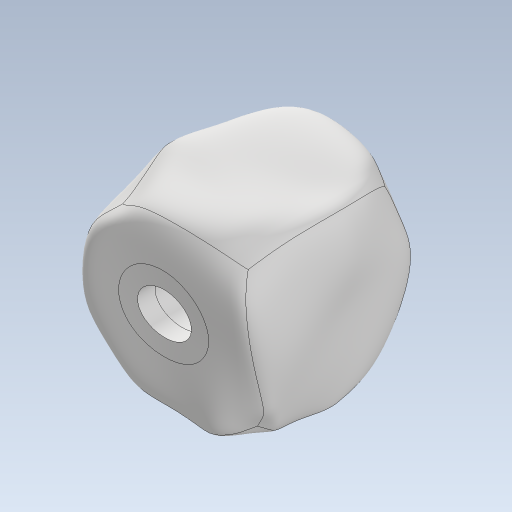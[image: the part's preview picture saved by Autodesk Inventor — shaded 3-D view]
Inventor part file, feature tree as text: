
AUTODESK INVENTOR PART (.ipt)
format: ipt  version: 2023 (Build 270158030, 158C)  size: 744,960 bytes
history: native  units: mm
features: other x4, plane x2, revolve x1, surface_op x1, extrude x1, chamfer x1, sketch x1, reference x1
ambient origin geometry x8: Origin, YZ Plane, XZ Plane, XY Plane, X Axis, Y Axis, Z Axis, Center Point
bodies: Solid1 (feature_tree), Solid4 (feature_tree)
feature tree (12):
  revolve  "Revolution1"  [1 undecoded]
  plane  "Work Plane1"
  plane  "Work Plane2"
  other  "Form7"
  surface_op  "Replace Face4"
  extrude  "Extrusion1"  TaperAngle=90.0deg  [1 undecoded]
  chamfer  "Chamfer2"  Distance=30.0mm
  sketch  "Sketch1"  dims[d0=25.0mm d1=12.0mm d2=90.0deg d4=30.0mm d5=0.0mm d6=2.5mm d7=3.0mm d17=2.0mm d18=2.0mm d19=45.0deg]
  reference  "Reference1"
  other  "<userpath>\Documents\0004-inventor\3D-CAD-main\trebuchet\trebuchet-assembly.iam"
  other  "trebuchet-assembly.iam"
  other  "V1_baseplate:1"
note: 2 required parameter values undecoded (feature->parameter linkage not recoverable at this tier; creation-order binding heuristic only, values carry confidence <= 0.55)